# Revit family: RN 15106 Valvola di ritegno EA
name_source: partatom
category: Rohrzubehör
units: mm (PartAtom-declared; Revit-internal decimal feet)

## family parameters
Arbeitsebenenbasiert = Nein
Beim Laden mit Abzugskörper schneiden = Nein
Bemaßung runder Anschluss = Durchmesser verwenden
Gemeinsam genutzt = Nein
Immer vertikal = Ja
Teiletyp = Ventil - Zerlegung in

## types (3) — shared parameters
1.010.00.2 Blattnummer der Richtlinie = 17
1.010.00.3 Ausgabedatum (Monat) der Richtlinie = 201601
1.010.00.4 Herstellername = R. Nussbaum AG
1.010.00.5 Revisionsdatum der Datei = 20190528
1.010.00.6 Webadresse des Herstellers = http://www.nussbaum.ch
1.100.00.3 Sortiernummer für Anzeigereihenfolge = 4
1.100.00.4 Produktbezeichnung = Sicherungs- und Ringleitungsarmaturen
1.960/3L.00.8 Link (URL) = https://www.nussbaum.ch
17.700.00.4 Armaturentyp = 6
17.700.00.7 Maximale Betriebstemperatur TB [°C] = 90
17.700.00.8 Maximaler Betriebsdruck (Arbeitsdruck) ps [1.0 · 105 Pa] = 16
Connector Visibility = Nein
EnclosingSpace Visibility = Nein
Hersteller = R. Nussbauzm AG
URL = https://www.nussbaum.ch

## per-type parameters (varying)
- DN 20: 1.800.00.3 TGA-Nummer=0040180000000000000000000000020070000000000000000100000000; 1.810.00.3 Hersteller-Bestellnummer=15106.05; 1.810.00.4 DATANORM-Nummer=15106.05; 1.810.00.5 StLB-Nummer=614.574; 1.810.00.6 GTIN-Nummer=7612945737311; 17.700.00.30 Produktbeschreibung=15106.05, Rückflussverhinderer EA, mit Innengewinde, DN=20, Rp=¾; 17.700.00.5 Nennweite DN=20; 17.700.00.6 kvs-Wert [m3/h]=10.8; CONNECTOR0_DIAMETER_dX_0r=20 mm  [stored 0.0656168 ft]; CONNECTOR0_dX_00=51 mm; CONNECTOR0_dX_01=36 mm; CONNECTOR0_ref_dX=36 mm; CONNECTOR1_DIAMETER_dX_0r=20 mm  [stored 0.0656168 ft]; CONNECTOR1_dX_00=19 mm; CONNECTOR1_dX_01=34 mm; CONNECTOR1_ref_dX=19 mm; CONNECTOR2_DIAMETER_dZ_0r=20 mm  [stored 0.0656168 ft]; CONNECTOR2_dZ_00=45 mm; CONNECTOR2_dZ_01=30 mm; CONNECTOR2_ref_dX=4 mm  [stored 0.0131234 ft]; CONNECTOR2_ref_dZ=30 mm; Modell=15106.05; R. Nussbaum AG 15106.05 de Visibility=Ja; R. Nussbaum AG 15106.06 de Visibility=Nein; R. Nussbaum AG 15106.07 de Visibility=Nein; Typenkommentare=Valvola di ritegno EADN 20
- DN 25: 1.800.00.3 TGA-Nummer=0040180000000000000000000000020070000000000000000200000000; 1.810.00.3 Hersteller-Bestellnummer=15106.06; 1.810.00.4 DATANORM-Nummer=15106.06; 1.810.00.5 StLB-Nummer=614.575; 1.810.00.6 GTIN-Nummer=7612945737625; 17.700.00.30 Produktbeschreibung=15106.06, Rückflussverhinderer EA, mit Innengewinde, DN=25, Rp=1; 17.700.00.5 Nennweite DN=25; 17.700.00.6 kvs-Wert [m3/h]=16.8; CONNECTOR0_DIAMETER_dX_0r=25 mm  [stored 0.082021 ft]; CONNECTOR0_dX_00=59 mm; CONNECTOR0_dX_01=42 mm; CONNECTOR0_ref_dX=42 mm; CONNECTOR1_DIAMETER_dX_0r=25 mm  [stored 0.082021 ft]; CONNECTOR1_dX_00=24 mm; CONNECTOR1_dX_01=41 mm; CONNECTOR1_ref_dX=24 mm; CONNECTOR2_DIAMETER_dZ_0r=28 mm; CONNECTOR2_dZ_00=50 mm; CONNECTOR2_dZ_01=35 mm; CONNECTOR2_ref_dX=5 mm  [stored 0.0164042 ft]; CONNECTOR2_ref_dZ=35 mm; Modell=15106.06; R. Nussbaum AG 15106.05 de Visibility=Nein; R. Nussbaum AG 15106.06 de Visibility=Ja; R. Nussbaum AG 15106.07 de Visibility=Nein; Typenkommentare=Valvola di ritegno EADN 25
- DN 32: 1.800.00.3 TGA-Nummer=0040180000000000000000000000020070000000000000000300000000; 1.810.00.3 Hersteller-Bestellnummer=15106.07; 1.810.00.4 DATANORM-Nummer=15106.07; 1.810.00.5 StLB-Nummer=614.576; 1.810.00.6 GTIN-Nummer=7612945735232; 17.700.00.30 Produktbeschreibung=15106.07, Rückflussverhinderer EA, mit Innengewinde, DN=32, Rp=1¼; 17.700.00.5 Nennweite DN=32; 17.700.00.6 kvs-Wert [m3/h]=31.2; CONNECTOR0_DIAMETER_dX_0r=32 mm; CONNECTOR0_dX_00=68 mm; CONNECTOR0_dX_01=49 mm; CONNECTOR0_ref_dX=49 mm; CONNECTOR1_DIAMETER_dX_0r=32 mm; CONNECTOR1_dX_00=28 mm; CONNECTOR1_dX_01=47 mm; CONNECTOR1_ref_dX=28 mm; CONNECTOR2_DIAMETER_dZ_0r=26 mm; CONNECTOR2_dZ_00=55 mm; CONNECTOR2_dZ_01=40 mm; CONNECTOR2_ref_dX=6 mm  [stored 0.019685 ft]; CONNECTOR2_ref_dZ=40 mm; Modell=15106.07; R. Nussbaum AG 15106.05 de Visibility=Nein; R. Nussbaum AG 15106.06 de Visibility=Nein; R. Nussbaum AG 15106.07 de Visibility=Ja; Typenkommentare=Valvola di ritegno EADN 32

note: [stored X ft] marks values corroborated as IEEE doubles in the binary element streams (Revit-internal decimal feet)

## geometry (parser evidence)
native form markers: Sweep x1
no freeform markers — native parametric forms only
